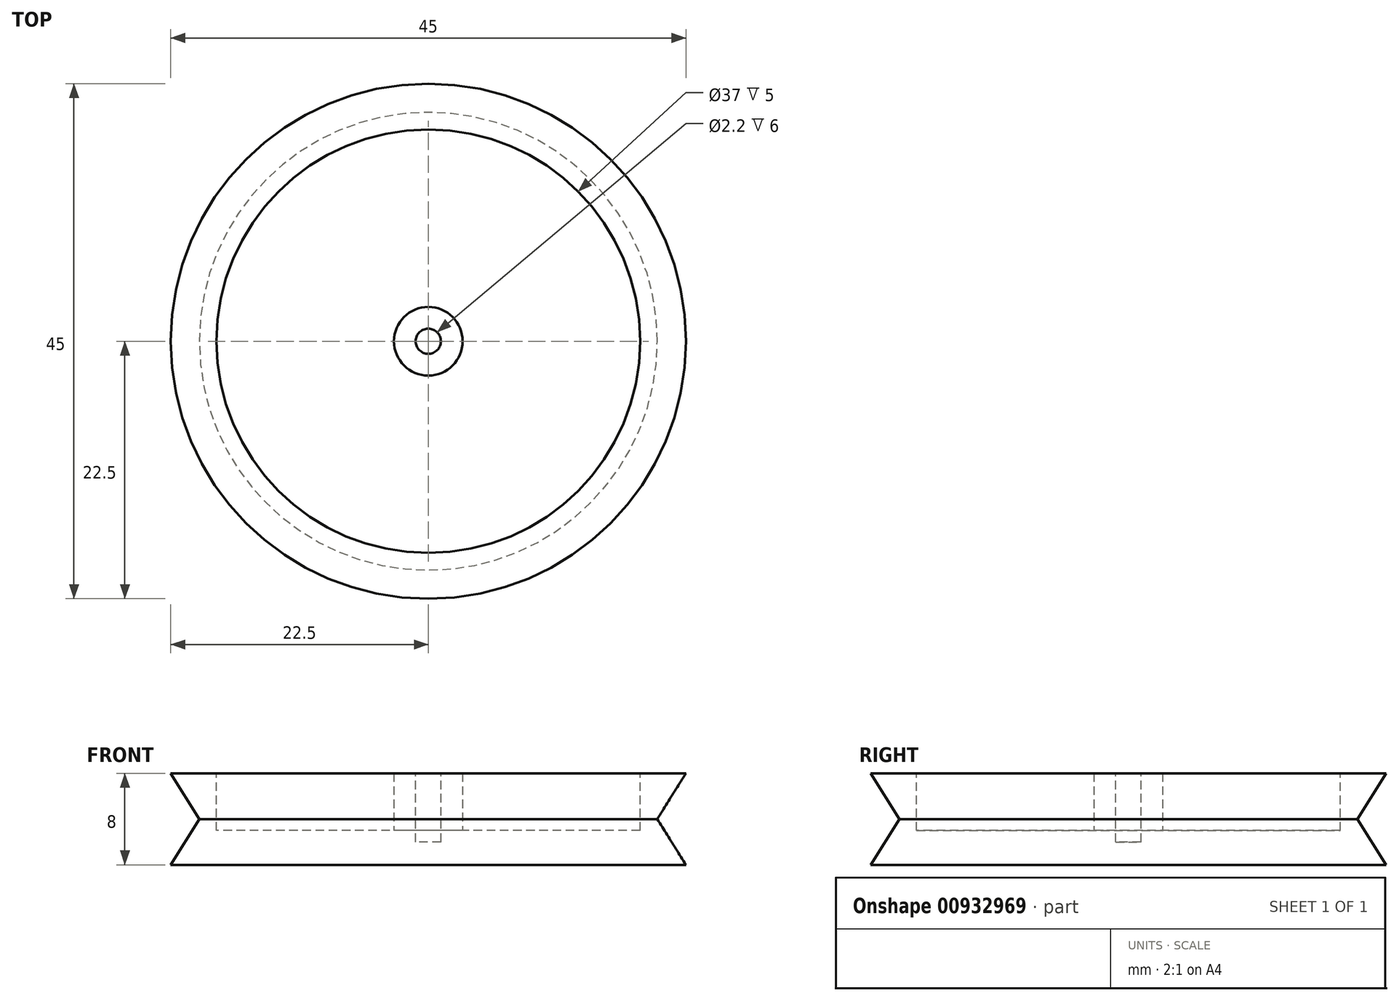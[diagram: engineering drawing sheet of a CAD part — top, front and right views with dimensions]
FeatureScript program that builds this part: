
annotation { "Feature Type Name" : "Feature", "Feature Type Description" : "" }
export const myFeature = defineFeature(function(context is Context, id is Id, definition is map)
    precondition{}
    {
        {
            var Q0;
            Q0=qCreatedBy(makeId("Top.planeOp"),FACE);
            var sketch = newSketch(context, id + "F0", { "sketchPlane" : qUnion([Q0])});
            skCircle(sketch, "E0", {"center": v(0, 0) * mm, "radius": 22.5 * mm});
            skSolve(sketch);
        }
        {
            var Q0;
            Q0=qCreatedBy(makeId("Front.planeOp"),FACE);
            var sketch = newSketch(context, id + "F1", { "sketchPlane" : qUnion([Q0])});
            skLineSegment(sketch, "E1.0", {"start": v(-22.5, 0) * mm, "end": v(22.5, 0) * mm});
            skLineSegment(sketch, "E2", {"start": v(0, 0) * mm, "end": v(22.5, 0) * mm});
            skLineSegment(sketch, "E3", {"start": v(22.5, 8) * mm, "end": v(0, 8) * mm});
            skLineSegment(sketch, "E4", {"start": v(0, 8) * mm, "end": v(0, 0) * mm});
            skLineSegment(sketch, "E5", {"start": v(0, 4) * mm, "end": v(34.73, 4) * mm, "construction": true});
            skLineSegment(sketch, "E6", {"start": v(22.5, 0) * mm, "end": v(20, 4) * mm});
            skLineSegment(sketch, "E7", {"start": v(20, 4) * mm, "end": v(22.5, 8) * mm});
            skSolve(sketch);
        }
        {
            var Q0;
            Q0 = qSketchRegion(id + "F1", true);
            var Q1;
            Q1=sQuery(id+"F1.wireOp",EDGE,"E4");
            revolve(context, id + "F2", {"surfaceOperationType" : NewSurfaceOperationType.NEW, "entities" : qUnion([Q0]), "axis" : qUnion([Q1]), "revolveType" : RevolveType.FULL});
        }
        {
            var Q0;
            Q0=makeQuery(id+"F2.opRevolve","SWEPT_FACE",FACE,{"disambiguationData":[OSD([sQuery(id+"F1.wireOp",EDGE,"E3")])]});
            var sketch = newSketch(context, id + "F3", { "sketchPlane" : qUnion([Q0])});
            skCircle(sketch, "E8", {"center": v(0, 0) * mm, "radius": 18.5 * mm});
            skSolve(sketch);
        }
        {
            var Q0;
            Q0=makeQuery(id+"F3.imprint","IMPRINT",FACE,{"disambiguationData":[TD([[makeQuery(id+"F3.imprint","IMPRINT",EDGE,{"derivedFrom":sQuery(id+"F3.wireOp",EDGE,"E8")}),1.0]])]});
            extrude(context, id + "F4", {"entities" : qUnion([Q0]), "operationType" : NewBodyOperationType.REMOVE, "oppositeDirection" : true, "depth" : 5 * mm, "offsetDistance" : 25 * mm});
        }
        {
            var Q0;
            Q0=makeQuery(id+"F4.boolean.opBoolean","COPY",FACE,{"derivedFrom":makeQuery(id+"F4.opExtrude","CAP_FACE",FACE,{"disambiguationData":[OSD([sQuery(id+"F3.wireOp",EDGE,"E8")])],"isStart":false})});
            var sketch = newSketch(context, id + "F5", { "sketchPlane" : qUnion([Q0])});
            skCircle(sketch, "E9", {"center": v(0, 0) * mm, "radius": 3 * mm});
            skSolve(sketch);
        }
        {
            var Q0;
            Q0=makeQuery(id+"F5.imprint","IMPRINT",FACE,{"disambiguationData":[TD([[makeQuery(id+"F5.imprint","IMPRINT",EDGE,{"derivedFrom":sQuery(id+"F5.wireOp",EDGE,"E9")}),1.0]])]});
            var Q1;
            Q1=makeQuery(id+"F2.opRevolve","SWEPT_FACE",FACE,{"disambiguationData":[OSD([sQuery(id+"F1.wireOp",EDGE,"E3")])]});
            extrude(context, id + "F6", {"entities" : qUnion([Q0]), "operationType" : NewBodyOperationType.ADD, "endBound" : BoundingType.UP_TO_SURFACE, "depth" : 25 * mm, "endBoundEntityFace" : qUnion([Q1]), "offsetDistance" : 25 * mm});
        }
        {
            var Q0;
            Q0=makeQuery(id+"F6.opExtrude","CAP_FACE",FACE,{"disambiguationData":[OSD([sQuery(id+"F5.wireOp",EDGE,"E9")])],"isStart":false});
            var sketch = newSketch(context, id + "F7", { "sketchPlane" : qUnion([Q0])});
            skCircle(sketch, "E10", {"center": v(0, 0) * mm, "radius": 1.1 * mm});
            skSolve(sketch);
        }
        {
            var Q0;
            Q0=makeQuery(id+"F7.imprint","IMPRINT",FACE,{"disambiguationData":[TD([[makeQuery(id+"F7.imprint","IMPRINT",EDGE,{"derivedFrom":sQuery(id+"F7.wireOp",EDGE,"E10")}),1.0]])]});
            extrude(context, id + "F8", {"entities" : qUnion([Q0]), "operationType" : NewBodyOperationType.REMOVE, "oppositeDirection" : true, "depth" : 6 * mm, "offsetDistance" : 25 * mm});
        }
    });
